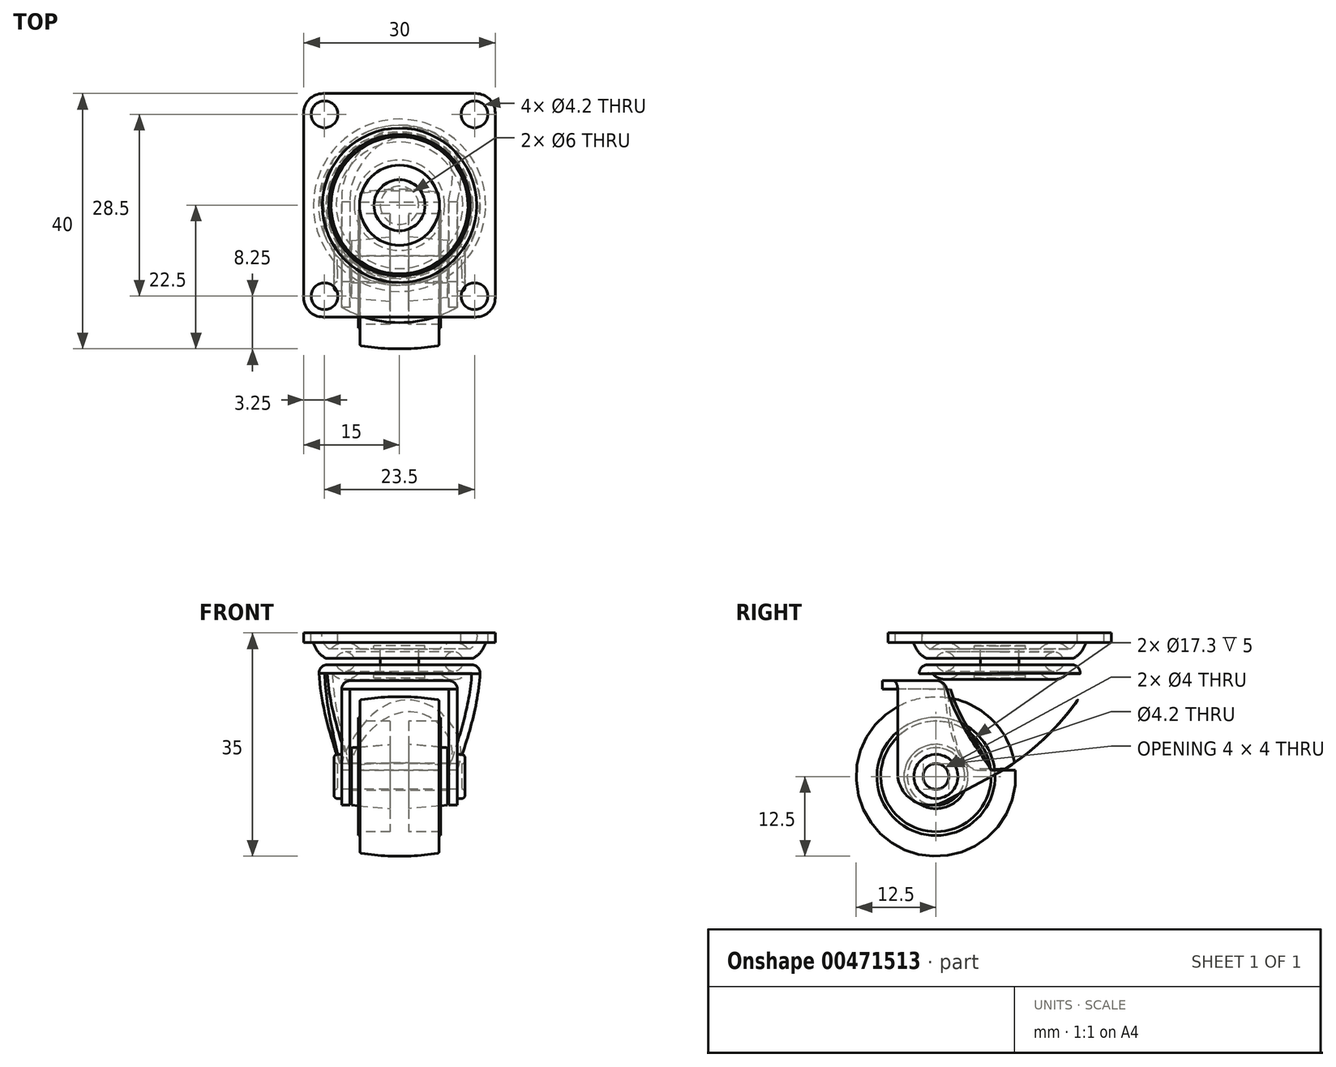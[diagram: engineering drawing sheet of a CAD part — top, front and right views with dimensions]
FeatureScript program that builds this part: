
annotation { "Feature Type Name" : "Feature", "Feature Type Description" : "" }
export const myFeature = defineFeature(function(context is Context, id is Id, definition is map)
    precondition{}
    {
        {
            var Q0;
            Q0=qCreatedBy(makeId("Top.planeOp"),FACE);
            var sketch = newSketch(context, id + "F0", { "sketchPlane" : qUnion([Q0])});
            skLineSegment(sketch, "E0.bottom", {"start": v(15, 17.5) * mm, "end": v(-15, 17.5) * mm});
            skLineSegment(sketch, "E0.top", {"start": v(15, -17.5) * mm, "end": v(-15, -17.5) * mm});
            skLineSegment(sketch, "E0.left", {"start": v(15, 17.5) * mm, "end": v(15, -17.5) * mm});
            skLineSegment(sketch, "E0.right", {"start": v(-15, 17.5) * mm, "end": v(-15, -17.5) * mm});
            skPoint(sketch, "E0.middle", {"position": v(0, 0) * mm});
            skSolve(sketch);
        }
        {
            var Q0;
            Q0=makeQuery(id+"F0.imprint","IMPRINT",FACE,{"disambiguationData":[TD([[makeQuery(id+"F0.imprint","IMPRINT",EDGE,{"derivedFrom":sQuery(id+"F0.wireOp",EDGE,"E0.bottom")}),1.0]])]});
            extrude(context, id + "F1", {"entities" : qUnion([Q0]), "oppositeDirection" : true, "depth" : 1.5 * mm});
        }
        {
            var Q0;
            Q0=qCreatedBy(makeId("Right.planeOp"),FACE);
            var sketch = newSketch(context, id + "F2", { "sketchPlane" : qUnion([Q0])});
            skLineSegment(sketch, "E1", {"start": v(0, -4) * mm, "end": v(0, 0) * mm});
            skLineSegment(sketch, "E2", {"start": v(-11.5, -4) * mm, "end": v(0, -4) * mm});
            skLineSegment(sketch, "E3", {"start": v(-13.5, -1.5) * mm, "end": v(-11.5, -4) * mm, "construction": true});
            skArc(sketch, "E4", {"start": v(-13.5, -1.5) * mm, "mid": v(-12.76, -2.96) * mm, "end": v(-11.5, -4) * mm});
            skLineSegment(sketch, "E5.0", {"start": v(17.5, -1.5) * mm, "end": v(-17.5, -1.5) * mm});
            skSolve(sketch);
        }
        {
            var Q0;
            {var subQ0=sQuery(id+"F2.wireOp",EDGE,"E2");Q0=makeQuery(id+"F2.imprint","IMPRINT",FACE,{"disambiguationData":[TD([[makeQuery(id+"F2.imprint","IMPRINT",EDGE,{"derivedFrom":subQ0}),1.0]])]});}
            var Q1;
            Q1=sQuery(id+"F2.wireOp",EDGE,"E1");
            revolve(context, id + "F3", {"operationType" : NewBodyOperationType.ADD, "entities" : qUnion([Q0]), "axis" : qUnion([Q1]), "revolveType" : RevolveType.FULL});
        }
        {
            var Q0;
            Q0=makeQuery(id+"F1.opExtrude","CAP_FACE",FACE,{"disambiguationData":[OSD([sQuery(id+"F0.wireOp",EDGE,"E0.bottom"),sQuery(id+"F0.wireOp",EDGE,"E0.top"),sQuery(id+"F0.wireOp",EDGE,"E0.left"),sQuery(id+"F0.wireOp",EDGE,"E0.right")])],"isStart":true});
            var sketch = newSketch(context, id + "F4", { "sketchPlane" : qUnion([Q0])});
            skLineSegment(sketch, "E6.bottom", {"start": v(-11.75, 14.25) * mm, "end": v(11.75, 14.25) * mm, "construction": true});
            skLineSegment(sketch, "E6.top", {"start": v(-11.75, -14.25) * mm, "end": v(11.75, -14.25) * mm, "construction": true});
            skLineSegment(sketch, "E6.left", {"start": v(-11.75, 14.25) * mm, "end": v(-11.75, -14.25) * mm, "construction": true});
            skLineSegment(sketch, "E6.right", {"start": v(11.75, 14.25) * mm, "end": v(11.75, -14.25) * mm, "construction": true});
            skPoint(sketch, "E6.middle", {"position": v(0, 0) * mm});
            skCircle(sketch, "E7", {"center": v(-11.75, 14.25) * mm, "radius": 2.1 * mm});
            skCircle(sketch, "E8", {"center": v(11.75, 14.25) * mm, "radius": 2.1 * mm});
            skCircle(sketch, "E9", {"center": v(-11.75, -14.25) * mm, "radius": 2.1 * mm});
            skCircle(sketch, "E10", {"center": v(11.75, -14.25) * mm, "radius": 2.1 * mm});
            skSolve(sketch);
        }
        {
            var Q0;
            Q0=makeQuery(id+"F4.imprint","IMPRINT",FACE,{"disambiguationData":[TD([[makeQuery(id+"F4.imprint","IMPRINT",EDGE,{"derivedFrom":sQuery(id+"F4.wireOp",EDGE,"E9")}),1.0]])]});
            var Q1;
            Q1=makeQuery(id+"F4.imprint","IMPRINT",FACE,{"disambiguationData":[TD([[makeQuery(id+"F4.imprint","IMPRINT",EDGE,{"derivedFrom":sQuery(id+"F4.wireOp",EDGE,"E10")}),1.0]])]});
            var Q2;
            Q2=makeQuery(id+"F4.imprint","IMPRINT",FACE,{"disambiguationData":[TD([[makeQuery(id+"F4.imprint","IMPRINT",EDGE,{"derivedFrom":sQuery(id+"F4.wireOp",EDGE,"E8")}),1.0]])]});
            var Q3;
            Q3=makeQuery(id+"F4.imprint","IMPRINT",FACE,{"disambiguationData":[TD([[makeQuery(id+"F4.imprint","IMPRINT",EDGE,{"derivedFrom":sQuery(id+"F4.wireOp",EDGE,"E7")}),1.0]])]});
            extrude(context, id + "F5", {"entities" : qUnion([Q0, Q1, Q2, Q3]), "operationType" : NewBodyOperationType.REMOVE, "endBound" : BoundingType.THROUGH_ALL, "oppositeDirection" : true, "depth" : 25 * mm});
        }
        {
            var Q0;
            Q0=makeQuery(id+"F1.opExtrude","SWEPT_EDGE",EDGE,{"disambiguationData":[OSD([sQuery(id+"F0.wireOp",EDGE,"E0.top"),sQuery(id+"F0.wireOp",EDGE,"E0.right")])]});
            var Q1;
            Q1=makeQuery(id+"F1.opExtrude","SWEPT_EDGE",EDGE,{"disambiguationData":[OSD([sQuery(id+"F0.wireOp",EDGE,"E0.top"),sQuery(id+"F0.wireOp",EDGE,"E0.left")])]});
            var Q2;
            Q2=makeQuery(id+"F1.opExtrude","SWEPT_EDGE",EDGE,{"disambiguationData":[OSD([sQuery(id+"F0.wireOp",EDGE,"E0.bottom"),sQuery(id+"F0.wireOp",EDGE,"E0.left")])]});
            var Q3;
            Q3=makeQuery(id+"F1.opExtrude","SWEPT_EDGE",EDGE,{"disambiguationData":[OSD([sQuery(id+"F0.wireOp",EDGE,"E0.bottom"),sQuery(id+"F0.wireOp",EDGE,"E0.right")])]});
            fillet(context, id + "F6", {"entities" : qUnion([Q0, Q1, Q2, Q3]), "radius" : 3 * mm, "tangentPropagation" : true, "allowEdgeOverflow" : false});
        }
        {
            var Q0;
            Q0=qCreatedBy(makeId("Front.planeOp"),FACE);
            cPlane(context, id + "F7", {"entities" : qUnion([Q0]), "cplaneType" : CPlaneType.OFFSET, "offset" : 10 * mm, "width" : 150 * mm, "height" : 150 * mm});
        }
        {
            var Q0;
            Q0=qCreatedBy(id+"F7.planeOp",FACE);
            var sketch = newSketch(context, id + "F8", { "sketchPlane" : qUnion([Q0])});
            skArc(sketch, "E11", {"start": v(6.2, -10.5) * mm, "mid": v(0, -10) * mm, "end": v(-6.21, -10.5) * mm});
            skLineSegment(sketch, "E12", {"start": v(-6.46, -13.85) * mm, "end": v(-1.46, -13.85) * mm});
            skLineSegment(sketch, "E13", {"start": v(-7.5, -22.5) * mm, "end": v(7.5, -22.5) * mm});
            skLineSegment(sketch, "E14", {"start": v(1.46, -13.85) * mm, "end": v(6.46, -13.85) * mm});
            skLineSegment(sketch, "E15", {"start": v(-1.46, -13.85) * mm, "end": v(-1.46, -17.47) * mm});
            skLineSegment(sketch, "E16", {"start": v(-7.5, -18) * mm, "end": v(-7.5, -22.5) * mm});
            skLineSegment(sketch, "E17", {"start": v(1.46, -13.85) * mm, "end": v(1.46, -17.47) * mm});
            skLineSegment(sketch, "E18", {"start": v(7.5, -18) * mm, "end": v(7.5, -22.5) * mm});
            skLineSegment(sketch, "E19", {"start": v(0, 0) * mm, "end": v(0, -32.65) * mm, "construction": true});
            skLineSegment(sketch, "E20", {"start": v(-6.21, -10.5) * mm, "end": v(-6.21, -13.25) * mm});
            skLineSegment(sketch, "E21", {"start": v(-6.21, -13.25) * mm, "end": v(-6.46, -13.25) * mm});
            skLineSegment(sketch, "E22", {"start": v(-6.46, -13.25) * mm, "end": v(-6.46, -13.85) * mm});
            skLineSegment(sketch, "E23", {"start": v(6.2, -10.5) * mm, "end": v(6.2, -13.25) * mm});
            skLineSegment(sketch, "E24", {"start": v(6.21, -13.25) * mm, "end": v(6.46, -13.25) * mm});
            skLineSegment(sketch, "E25", {"start": v(6.46, -13.25) * mm, "end": v(6.46, -13.85) * mm});
            skLineSegment(sketch, "E26", {"start": v(-7.5, -18) * mm, "end": v(-1.46, -17.47) * mm});
            skLineSegment(sketch, "E27", {"start": v(7.5, -18) * mm, "end": v(1.46, -17.47) * mm});
            skSolve(sketch);
        }
        {
            var Q0;
            Q0=makeQuery(id+"F8.imprint","IMPRINT",FACE,{"disambiguationData":[TD([[makeQuery(id+"F8.imprint","IMPRINT",EDGE,{"derivedFrom":sQuery(id+"F8.wireOp",EDGE,"E11")}),1.0]])]});
            var Q1;
            Q1=sQuery(id+"F8.wireOp",EDGE,"E13");
            revolve(context, id + "F9", {"entities" : qUnion([Q0]), "axis" : qUnion([Q1]), "revolveType" : RevolveType.FULL});
        }
        {
            var Q0;
            Q0=makeQuery(id+"F9.opRevolve","SWEPT_FACE",FACE,{"disambiguationData":[OSD([sQuery(id+"F8.wireOp",EDGE,"E18")])]});
            var sketch = newSketch(context, id + "F10", { "sketchPlane" : qUnion([Q0])});
            skCircle(sketch, "E28", {"center": v(-10, -22.5) * mm, "radius": 2.1 * mm});
            skSolve(sketch);
        }
        {
            var Q0;
            Q0=makeQuery(id+"F10.imprint","IMPRINT",FACE,{"disambiguationData":[TD([[makeQuery(id+"F10.imprint","IMPRINT",EDGE,{"derivedFrom":sQuery(id+"F10.wireOp",EDGE,"E28")}),1.0]])]});
            extrude(context, id + "F11", {"entities" : qUnion([Q0]), "operationType" : NewBodyOperationType.REMOVE, "endBound" : BoundingType.THROUGH_ALL, "oppositeDirection" : true, "depth" : 25 * mm});
        }
        {
            var Q0;
            Q0=makeQuery(id+"F9.opRevolve","SWEPT_EDGE",EDGE,{"disambiguationData":[OSD([sQuery(id+"F8.wireOp",EDGE,"E11"),sQuery(id+"F8.wireOp",EDGE,"E23")])]});
            var Q1;
            Q1=makeQuery(id+"F9.opRevolve","SWEPT_EDGE",EDGE,{"disambiguationData":[OSD([sQuery(id+"F8.wireOp",EDGE,"E11"),sQuery(id+"F8.wireOp",EDGE,"E20")])]});
            fillet(context, id + "F12", {"entities" : qUnion([Q0, Q1]), "radius" : 0.3 * mm, "tangentPropagation" : true, "allowEdgeOverflow" : false});
        }
        {
            var Q0;
            Q0=makeQuery(id+"F1.opExtrude","CAP_FACE",FACE,{"disambiguationData":[OSD([sQuery(id+"F0.wireOp",EDGE,"E0.bottom"),sQuery(id+"F0.wireOp",EDGE,"E0.top"),sQuery(id+"F0.wireOp",EDGE,"E0.left"),sQuery(id+"F0.wireOp",EDGE,"E0.right")])],"isStart":true});
            cPlane(context, id + "F13", {"entities" : qUnion([Q0]), "cplaneType" : CPlaneType.OFFSET, "offset" : 5 * mm, "oppositeDirection" : true, "width" : 150 * mm, "height" : 150 * mm});
        }
        {
            var Q0;
            Q0=qCreatedBy(id+"F13.planeOp",FACE);
            var sketch = newSketch(context, id + "F14", { "sketchPlane" : qUnion([Q0])});
            skCircle(sketch, "E29", {"center": v(0, 0) * mm, "radius": 12.65 * mm});
            skSolve(sketch);
        }
        {
            var Q0;
            Q0=qCreatedBy(id+"F13.planeOp",FACE);
            cPlane(context, id + "F15", {"entities" : qUnion([Q0]), "cplaneType" : CPlaneType.OFFSET, "offset" : 15 * mm, "oppositeDirection" : true, "width" : 150 * mm, "height" : 150 * mm});
        }
        {
            var Q0;
            Q0=qCreatedBy(id+"F15.planeOp",FACE);
            var sketch = newSketch(context, id + "F16", { "sketchPlane" : qUnion([Q0])});
            skArc(sketch, "E30", {"start": v(-9.05, -3.6) * mm, "mid": v(0, -12.65) * mm, "end": v(9.05, -3.6) * mm});
            skArc(sketch, "E31", {"start": v(9.05, 3.6) * mm, "mid": v(0, 12.65) * mm, "end": v(-9.05, 3.6) * mm});
            skLineSegment(sketch, "E32", {"start": v(-9.05, -3.6) * mm, "end": v(-9.05, 3.6) * mm});
            skLineSegment(sketch, "E33", {"start": v(9.05, -3.6) * mm, "end": v(9.05, 3.6) * mm});
            skSolve(sketch);
        }
        {
            var Q0;
            Q0=qCreatedBy(id+"F13.planeOp",FACE);
            cPlane(context, id + "F17", {"entities" : qUnion([Q0]), "cplaneType" : CPlaneType.OFFSET, "offset" : 3 * mm, "oppositeDirection" : true, "width" : 150 * mm, "height" : 150 * mm});
        }
        {
            var Q0;
            Q0=qCreatedBy(id+"F17.planeOp",FACE);
            var sketch = newSketch(context, id + "F18", { "sketchPlane" : qUnion([Q0])});
            skCircle(sketch, "E34", {"center": v(0, 0) * mm, "radius": 12.65 * mm});
            skSolve(sketch);
        }
        {
            var Q0;
            Q0=makeQuery(id+"F14.imprint","IMPRINT",FACE,{"disambiguationData":[TD([[makeQuery(id+"F14.imprint","IMPRINT",EDGE,{"derivedFrom":sQuery(id+"F14.wireOp",EDGE,"E29")}),1.0]])]});
            var Q1;
            Q1=makeQuery(id+"F18.imprint","IMPRINT",FACE,{"disambiguationData":[TD([[makeQuery(id+"F18.imprint","IMPRINT",EDGE,{"derivedFrom":sQuery(id+"F18.wireOp",EDGE,"E34")}),1.0]])]});
            var Q2;
            Q2=makeQuery(id+"F16.imprint","IMPRINT",FACE,{"disambiguationData":[TD([[makeQuery(id+"F16.imprint","IMPRINT",EDGE,{"derivedFrom":sQuery(id+"F16.wireOp",EDGE,"E30")}),1.0]])]});
            loft(context, id + "F19", {"endCondition" : LoftEndDerivativeType.TANGENT_TO_PROFILE, "endMagnitude" : 0.5, "sheetProfilesArray" : [{ "sheetProfileEntities" : qUnion([Q0]) }, { "sheetProfileEntities" : qUnion([Q1]) }, { "sheetProfileEntities" : qUnion([Q2]) }]});
        }
        {
            var Q0;
            Q0=makeQuery(id+"F19.opLoft","SWEPT_BODY",BODY,{"disambiguationData":[OSD([makeQuery(id+"F14.imprint","IMPRINT",FACE,{"disambiguationData":[TD([[makeQuery(id+"F14.imprint","IMPRINT",EDGE,{"derivedFrom":sQuery(id+"F14.wireOp",EDGE,"E29")}),1.0]])]}),makeQuery(id+"F16.imprint","IMPRINT",FACE,{"disambiguationData":[TD([[makeQuery(id+"F16.imprint","IMPRINT",EDGE,{"derivedFrom":sQuery(id+"F16.wireOp",EDGE,"E30")}),1.0]])]}),sQuery(id+"F18.wireOp",EDGE,"E34")])]});
            deleteBodies(context, id + "F20", {"entities" : qUnion([Q0])});
        }
        {
            var Q0;
            Q0=qCreatedBy(makeId("Right.planeOp"),FACE);
            var sketch = newSketch(context, id + "F21", { "sketchPlane" : qUnion([Q0])});
            skLineSegment(sketch, "E35", {"start": v(0.5, -7.5) * mm, "end": v(-16, -7.5) * mm});
            skLineSegment(sketch, "E36", {"start": v(-16, -7.5) * mm, "end": v(-16, -22) * mm});
            skLineSegment(sketch, "E37", {"start": v(-16, -27) * mm, "end": v(-4.2, -27) * mm});
            skLineSegment(sketch, "E38", {"start": v(0.5, -21.5) * mm, "end": v(0.5, -7.5) * mm});
            skArc(sketch, "E39", {"start": v(-16, -22) * mm, "mid": v(-13.57, -26.3) * mm, "end": v(-8.63, -26.4) * mm});
            skLineSegment(sketch, "E40", {"start": v(0.5, -21.5) * mm, "end": v(-8.63, -26.4) * mm});
            skLineSegment(sketch, "E41", {"start": v(-16, -21.5) * mm, "end": v(0.5, -21.5) * mm, "construction": true});
            skPoint(sketch, "E42.0", {"position": v(-17.5, -1.5) * mm});
            skSolve(sketch);
        }
        {
            var Q0;
            Q0=makeQuery(id+"F21.imprint","IMPRINT",FACE,{"disambiguationData":[TD([[makeQuery(id+"F21.imprint","IMPRINT",EDGE,{"derivedFrom":sQuery(id+"F21.wireOp",EDGE,"E35")}),1.0]])]});
            extrude(context, id + "F22", {"entities" : qUnion([Q0]), "endBound" : BoundingType.SYMMETRIC, "depth" : 18.1 * mm});
        }
        {
            var Q0;
            Q0=makeQuery(id+"F1.opExtrude","CAP_FACE",FACE,{"disambiguationData":[OSD([sQuery(id+"F0.wireOp",EDGE,"E0.bottom"),sQuery(id+"F0.wireOp",EDGE,"E0.top"),sQuery(id+"F0.wireOp",EDGE,"E0.left"),sQuery(id+"F0.wireOp",EDGE,"E0.right")])],"isStart":true});
            cPlane(context, id + "F23", {"entities" : qUnion([Q0]), "cplaneType" : CPlaneType.OFFSET, "offset" : 5 * mm, "oppositeDirection" : true, "width" : 150 * mm, "height" : 150 * mm});
        }
        {
            var Q0;
            Q0=qCreatedBy(id+"F23.planeOp",FACE);
            var sketch = newSketch(context, id + "F24", { "sketchPlane" : qUnion([Q0])});
            skCircle(sketch, "E43", {"center": v(0, 0) * mm, "radius": 12.65 * mm});
            skSolve(sketch);
        }
        {
            var Q0;
            Q0=makeQuery(id+"F1.opExtrude","CAP_FACE",FACE,{"disambiguationData":[OSD([sQuery(id+"F0.wireOp",EDGE,"E0.bottom"),sQuery(id+"F0.wireOp",EDGE,"E0.top"),sQuery(id+"F0.wireOp",EDGE,"E0.left"),sQuery(id+"F0.wireOp",EDGE,"E0.right")])],"isStart":true});
            cPlane(context, id + "F25", {"entities" : qUnion([Q0]), "cplaneType" : CPlaneType.OFFSET, "offset" : 21.5 * mm, "oppositeDirection" : true, "width" : 150 * mm, "height" : 150 * mm});
        }
        {
            var Q0;
            Q0=qCreatedBy(id+"F25.planeOp",FACE);
            var sketch = newSketch(context, id + "F26", { "sketchPlane" : qUnion([Q0])});
            skPoint(sketch, "E44.middle", {"position": v(0, 0) * mm});
            skCircle(sketch, "E45", {"center": v(0, 0) * mm, "radius": 12.65 * mm, "construction": true});
            skLineSegment(sketch, "E46", {"start": v(-9.05, -3.6) * mm, "end": v(-9.05, 3.6) * mm});
            skLineSegment(sketch, "E47", {"start": v(9.05, -3.6) * mm, "end": v(9.05, 3.6) * mm});
            skLineSegment(sketch, "E48", {"start": v(0, -12.65) * mm, "end": v(0, 12.65) * mm, "construction": true});
            skArc(sketch, "E49", {"start": v(-9.05, -3.6) * mm, "mid": v(0, -12.65) * mm, "end": v(9.05, -3.6) * mm});
            skArc(sketch, "E50", {"start": v(-9.05, 3.6) * mm, "mid": v(0, 12.65) * mm, "end": v(9.05, 3.6) * mm});
            skSolve(sketch);
        }
        {
            var Q0;
            Q0 = qSketchRegion(id + "F24", true);
            var Q1;
            Q1 = qSketchRegion(id + "F26", true);
            loft(context, id + "F27", {"startCondition" : LoftEndDerivativeType.NORMAL_TO_PROFILE, "startMagnitude" : 1, "sheetProfilesArray" : [{ "sheetProfileEntities" : qUnion([Q0]) }, { "sheetProfileEntities" : qUnion([Q1]) }]});
        }
        {
            var Q0;
            Q0=makeQuery(id+"F27.opLoft","SWEPT_BODY",BODY,{"disambiguationData":[OSD([makeQuery(id+"F24.imprint","IMPRINT",FACE,{"disambiguationData":[TD([[makeQuery(id+"F24.imprint","IMPRINT",EDGE,{"derivedFrom":sQuery(id+"F24.wireOp",EDGE,"E43")}),1.0]])]}),makeQuery(id+"F26.imprint","IMPRINT",FACE,{"disambiguationData":[TD([[makeQuery(id+"F26.imprint","IMPRINT",EDGE,{"derivedFrom":sQuery(id+"F26.wireOp",EDGE,"E46")}),-1.0]])]})])]});
            var Q1;
            Q1=makeQuery(id+"F22.opExtrude","SWEPT_BODY",BODY,{"disambiguationData":[OSD([sQuery(id+"F21.wireOp",EDGE,"E35"),sQuery(id+"F21.wireOp",EDGE,"E36"),sQuery(id+"F21.wireOp",EDGE,"E38"),sQuery(id+"F21.wireOp",EDGE,"E39"),sQuery(id+"F21.wireOp",EDGE,"E40")])]});
            booleanBodies(context, id + "F28", {"operationType" : BooleanOperationType.UNION, "tools" : qUnion([Q0, Q1])});
        }
        {
            var Q0;
            Q0=makeQuery(id+"F27.opLoft","CAP_FACE",FACE,{"disambiguationData":[OSD([makeQuery(id+"F26.imprint","IMPRINT",FACE,{"disambiguationData":[TD([[makeQuery(id+"F26.imprint","IMPRINT",EDGE,{"derivedFrom":sQuery(id+"F26.wireOp",EDGE,"E46")}),-1.0]])]})])],"isStart":true});
            var Q1;
            Q1=makeQuery(id+"F22.opExtrude","SWEPT_FACE",FACE,{"disambiguationData":[OSD([sQuery(id+"F21.wireOp",EDGE,"E40")])]});
            var Q2;
            Q2=makeQuery(id+"F22.opExtrude","SWEPT_FACE",FACE,{"disambiguationData":[OSD([sQuery(id+"F21.wireOp",EDGE,"E39")])]});
            var Q3;
            Q3=makeQuery(id+"F22.opExtrude","SWEPT_FACE",FACE,{"disambiguationData":[OSD([sQuery(id+"F21.wireOp",EDGE,"E36")])]});
            shell(context, id + "F29", {"entities" : qUnion([Q0, Q1, Q2, Q3]), "thickness" : 1.3 * mm});
        }
        {
            var Q0;
            Q0=qCreatedBy(makeId("Right.planeOp"),FACE);
            var sketch = newSketch(context, id + "F30", { "sketchPlane" : qUnion([Q0])});
            skArc(sketch, "E51", {"start": v(0.5, -21.5) * mm, "mid": v(7.1, -16.43) * mm, "end": v(12.5, -10.1) * mm});
            skLineSegment(sketch, "E52.0", {"start": v(0.5, -21.5) * mm, "end": v(-8.63, -26.4) * mm, "construction": true});
            skLineSegment(sketch, "E53", {"start": v(12.5, -10.1) * mm, "end": v(14.5, -10.1) * mm});
            skLineSegment(sketch, "E54", {"start": v(14.5, -10.1) * mm, "end": v(14.5, -21.5) * mm});
            skLineSegment(sketch, "E55", {"start": v(14.5, -21.5) * mm, "end": v(0.5, -21.5) * mm});
            skSolve(sketch);
        }
        {
            var Q0;
            Q0=makeQuery(id+"F30.imprint","IMPRINT",FACE,{"disambiguationData":[TD([[makeQuery(id+"F30.imprint","IMPRINT",EDGE,{"derivedFrom":sQuery(id+"F30.wireOp",EDGE,"E51")}),-1.0]])]});
            extrude(context, id + "F31", {"entities" : qUnion([Q0]), "operationType" : NewBodyOperationType.REMOVE, "endBound" : BoundingType.SYMMETRIC, "oppositeDirection" : true, "depth" : 25 * mm});
        }
        {
            var Q0;
            Q0=makeQuery(id+"F22.opExtrude","SWEPT_FACE",FACE,{"disambiguationData":[OSD([sQuery(id+"F21.wireOp",EDGE,"E35")])]});
            var sketch = newSketch(context, id + "F32", { "sketchPlane" : qUnion([Q0])});
            skLineSegment(sketch, "E56.0", {"start": v(9.05, -16) * mm, "end": v(-9.05, -16) * mm});
            skArc(sketch, "E57", {"start": v(-9.05, -16) * mm, "mid": v(0, -18.38) * mm, "end": v(9.05, -16) * mm});
            skSolve(sketch);
        }
        {
            var Q0;
            Q0=makeQuery(id+"F32.imprint","IMPRINT",FACE,{"disambiguationData":[TD([[makeQuery(id+"F32.imprint","IMPRINT",EDGE,{"derivedFrom":sQuery(id+"F32.wireOp",EDGE,"E56.0")}),1.0]])]});
            var Q1;
            Q1=makeQuery(id+"F29.opShell","OFFSET_FACE",FACE,{"disambiguationData":[OSD([sQuery(id+"F21.wireOp",EDGE,"E35")])]});
            extrude(context, id + "F33", {"entities" : qUnion([Q0]), "operationType" : NewBodyOperationType.ADD, "endBound" : BoundingType.UP_TO_SURFACE, "oppositeDirection" : true, "endBoundEntityFace" : qUnion([Q1]), "depth" : 25 * mm});
        }
        {
            var Q0;
            Q0=makeQuery(id+"F27.opLoft","CAP_FACE",FACE,{"disambiguationData":[OSD([makeQuery(id+"F24.imprint","IMPRINT",FACE,{"disambiguationData":[TD([[makeQuery(id+"F24.imprint","IMPRINT",EDGE,{"derivedFrom":sQuery(id+"F24.wireOp",EDGE,"E43")}),1.0]])]})])],"isStart":true});
            var Q1;
            Q1=makeQuery(id+"F22.opExtrude","CAP_EDGE",EDGE,{"disambiguationData":[OSD([sQuery(id+"F21.wireOp",EDGE,"E35")])],"isStart":false});
            var Q2;
            Q2=makeQuery(id+"F22.opExtrude","CAP_EDGE",EDGE,{"disambiguationData":[OSD([sQuery(id+"F21.wireOp",EDGE,"E35")])],"isStart":true});
            fillet(context, id + "F34", {"entities" : qUnion([Q0, Q1, Q2]), "radius" : 1.3 * mm, "tangentPropagation" : true, "allowEdgeOverflow" : false});
        }
        {
            var Q0;
            Q0=qCreatedBy(id+"F7.planeOp",FACE);
            var sketch = newSketch(context, id + "F35", { "sketchPlane" : qUnion([Q0])});
            skLineSegment(sketch, "E58.0", {"start": v(-7.5, -20.4) * mm, "end": v(-7.5, -24.6) * mm});
            skLineSegment(sketch, "E59.0", {"start": v(7.5, -20.4) * mm, "end": v(7.5, -24.6) * mm});
            skLineSegment(sketch, "E60", {"start": v(-9.75, -22.5) * mm, "end": v(9.75, -22.5) * mm});
            skLineSegment(sketch, "E61", {"start": v(-9.05, -20.5) * mm, "end": v(9.05, -20.5) * mm});
            skPoint(sketch, "E62", {"position": v(-7.5, -22.5) * mm});
            skLineSegment(sketch, "E63", {"start": v(-9.05, -20.5) * mm, "end": v(-9.05, -19.05) * mm});
            skLineSegment(sketch, "E64", {"start": v(-9.05, -19.05) * mm, "end": v(-10.25, -19.05) * mm});
            skLineSegment(sketch, "E65", {"start": v(-10.25, -19.05) * mm, "end": v(-10.25, -20.5) * mm});
            skLineSegment(sketch, "E66.0.0", {"start": v(-9.05, -22) * mm, "end": v(-9.05, -8.8) * mm});
            skFitSpline(sketch, "E66.0.2", {"points": [v(-9.05, -21.5) * mm, v(-9.05, -17.27) * mm, v(-9.05, -13.03) * mm, v(-9.05, -8.8) * mm], "construction": true});
            skLineSegment(sketch, "E66.0.4", {"start": v(-9.05, -21.5) * mm, "end": v(-9.05, -26.4) * mm});
            skLineSegment(sketch, "E66.0.5", {"start": v(-9.05, -27) * mm, "end": v(-9.05, -22) * mm, "construction": true});
            skLineSegment(sketch, "E67.0", {"start": v(-9.05, -21.5) * mm, "end": v(-9.05, -26.4) * mm, "construction": true});
            skLineSegment(sketch, "E68", {"start": v(-10.25, -20.5) * mm, "end": v(-9.75, -20.5) * mm});
            skLineSegment(sketch, "E69", {"start": v(-9.75, -20.5) * mm, "end": v(-9.75, -22.5) * mm});
            skLineSegment(sketch, "E70", {"start": v(0, -7.68) * mm, "end": v(0, -37.41) * mm, "construction": true});
            skLineSegment(sketch, "E71.MirrorCS", {"start": v(10.25, -20.5) * mm, "end": v(9.75, -20.5) * mm});
            skLineSegment(sketch, "E72.MirrorCS", {"start": v(9.75, -20.5) * mm, "end": v(9.75, -22.5) * mm});
            skLineSegment(sketch, "E73.MirrorCS", {"start": v(10.25, -19.05) * mm, "end": v(10.25, -20.5) * mm});
            skLineSegment(sketch, "E74.MirrorCS", {"start": v(9.05, -20.5) * mm, "end": v(9.05, -19.05) * mm});
            skLineSegment(sketch, "E75.MirrorCS", {"start": v(9.05, -19.05) * mm, "end": v(10.25, -19.05) * mm});
            skSolve(sketch);
        }
        {
            var Q0;
            {var subQ4=sQuery(id+"F35.wireOp",EDGE,"E64");Q0=makeQuery(id+"F35.imprint","IMPRINT",FACE,{"disambiguationData":[TD([[makeQuery(id+"F35.imprint","IMPRINT",EDGE,{"derivedFrom":subQ4}),1.0]])]});}
            var Q1;
            {var subQ3=sQuery(id+"F35.wireOp",EDGE,"E66.0.4");var subQ10=makeQuery(id+"F35.imprint","IMPRINT",VERTEX,{"derivedFrom":subQ3});Q1=makeQuery(id+"F35.imprint","IMPRINT",FACE,{"disambiguationData":[TD([[makeQuery(id+"F35.imprint","IMPRINT",EDGE,{"disambiguationData":[TD([[subQ10,1.0]])],"derivedFrom":subQ3}),1.0]])]});}
            var Q2;
            {var subQ0=sQuery(id+"F35.wireOp",EDGE,"E60");var subQ1=sQuery(id+"F35.wireOp",EDGE,"E58.0");var subQ2=makeQuery(id+"F35.imprint","INTERSECT",VERTEX,{"derivedFrom":[subQ1,subQ0]});Q2=makeQuery(id+"F35.imprint","IMPRINT",FACE,{"disambiguationData":[TD([[makeQuery(id+"F35.imprint","IMPRINT",EDGE,{"disambiguationData":[TD([[subQ2,1.0]])],"derivedFrom":subQ1}),1.0]])]});}
            var Q3;
            Q3=makeQuery(id+"F35.imprint","IMPRINT",FACE,{"disambiguationData":[TD([[makeQuery(id+"F35.imprint","IMPRINT",EDGE,{"derivedFrom":sQuery(id+"F35.wireOp",EDGE,"E71.MirrorCS")}),-1.0]])]});
            var Q4;
            Q4=sQuery(id+"F35.wireOp",EDGE,"E60");
            revolve(context, id + "F36", {"entities" : qUnion([Q0, Q1, Q2, Q3]), "axis" : qUnion([Q4]), "revolveType" : RevolveType.FULL});
        }
        {
            var Q0;
            Q0=makeQuery(id+"F36.opRevolve","SWEPT_EDGE",EDGE,{"disambiguationData":[OSD([sQuery(id+"F35.wireOp",EDGE,"E73.MirrorCS"),sQuery(id+"F35.wireOp",EDGE,"E75.MirrorCS")])]});
            var Q1;
            Q1=makeQuery(id+"F36.opRevolve","SWEPT_EDGE",EDGE,{"disambiguationData":[OSD([sQuery(id+"F35.wireOp",EDGE,"E71.MirrorCS"),sQuery(id+"F35.wireOp",EDGE,"E73.MirrorCS")])]});
            var Q2;
            Q2=makeQuery(id+"F36.opRevolve","SWEPT_EDGE",EDGE,{"disambiguationData":[OSD([sQuery(id+"F35.wireOp",EDGE,"E65"),sQuery(id+"F35.wireOp",EDGE,"E68")])]});
            var Q3;
            Q3=makeQuery(id+"F36.opRevolve","SWEPT_EDGE",EDGE,{"disambiguationData":[OSD([sQuery(id+"F35.wireOp",EDGE,"E64"),sQuery(id+"F35.wireOp",EDGE,"E65")])]});
            fillet(context, id + "F37", {"entities" : qUnion([Q0, Q1, Q2, Q3]), "radius" : 0.5 * mm, "tangentPropagation" : true, "allowEdgeOverflow" : false});
        }
        {
            var Q0;
            Q0=makeQuery(id+"F36.opRevolve","SWEPT_BODY",BODY,{"disambiguationData":[OSD([sQuery(id+"F35.wireOp",EDGE,"E60"),sQuery(id+"F35.wireOp",EDGE,"E61"),sQuery(id+"F35.wireOp",EDGE,"E64"),sQuery(id+"F35.wireOp",EDGE,"E65"),sQuery(id+"F35.wireOp",EDGE,"E66.0.0"),sQuery(id+"F35.wireOp",EDGE,"E68"),sQuery(id+"F35.wireOp",EDGE,"E69"),sQuery(id+"F35.wireOp",EDGE,"E71.MirrorCS"),sQuery(id+"F35.wireOp",EDGE,"E72.MirrorCS"),sQuery(id+"F35.wireOp",EDGE,"E73.MirrorCS"),sQuery(id+"F35.wireOp",EDGE,"E74.MirrorCS"),sQuery(id+"F35.wireOp",EDGE,"E75.MirrorCS")])]});
            var Q1;
            Q1=makeQuery(id+"F27.opLoft","SWEPT_BODY",BODY,{"disambiguationData":[OSD([makeQuery(id+"F24.imprint","IMPRINT",FACE,{"disambiguationData":[TD([[makeQuery(id+"F24.imprint","IMPRINT",EDGE,{"derivedFrom":sQuery(id+"F24.wireOp",EDGE,"E43")}),1.0]])]}),makeQuery(id+"F26.imprint","IMPRINT",FACE,{"disambiguationData":[TD([[makeQuery(id+"F26.imprint","IMPRINT",EDGE,{"derivedFrom":sQuery(id+"F26.wireOp",EDGE,"E46")}),-1.0]])]})])]});
            booleanBodies(context, id + "F38", {"operationType" : BooleanOperationType.SUBTRACTION, "tools" : qUnion([Q0]), "targets" : qUnion([Q1]), "keepTools" : true});
        }
        {
            var Q0;
            Q0=makeQuery(id+"F3.opRevolve","SWEPT_FACE",FACE,{"disambiguationData":[OSD([sQuery(id+"F2.wireOp",EDGE,"E2")])]});
            var Q1;
            Q1=makeQuery(id+"F27.opLoft","CAP_FACE",FACE,{"disambiguationData":[OSD([makeQuery(id+"F24.imprint","IMPRINT",FACE,{"disambiguationData":[TD([[makeQuery(id+"F24.imprint","IMPRINT",EDGE,{"derivedFrom":sQuery(id+"F24.wireOp",EDGE,"E43")}),1.0]])]})])],"isStart":true});
            cPlane(context, id + "F39", {"entities" : qUnion([Q0, Q1]), "cplaneType" : CPlaneType.MID_PLANE, "offset" : 25 * mm, "width" : 150 * mm, "height" : 150 * mm});
        }
        {
            var Q0;
            Q0=qCreatedBy(id+"F39.planeOp",FACE);
            var sketch = newSketch(context, id + "F40", { "sketchPlane" : qUnion([Q0])});
            skArc(sketch, "E76", {"start": v(0, 7) * mm, "mid": v(1.5, 8.5) * mm, "end": v(0, 10) * mm});
            skLineSegment(sketch, "E77", {"start": v(0, 10) * mm, "end": v(0, 7) * mm});
            skSolve(sketch);
        }
        {
            var Q0;
            Q0=makeQuery(id+"F40.imprint","IMPRINT",FACE,{"disambiguationData":[TD([[makeQuery(id+"F40.imprint","IMPRINT",EDGE,{"derivedFrom":sQuery(id+"F40.wireOp",EDGE,"E76")}),1.0]])]});
            var Q1;
            Q1=sQuery(id+"F40.wireOp",EDGE,"E77");
            revolve(context, id + "F41", {"entities" : qUnion([Q0]), "axis" : qUnion([Q1]), "revolveType" : RevolveType.FULL});
        }
        {
            var Q0;
            Q0=makeQuery(id+"F41.opRevolve","SWEPT_BODY",BODY,{"disambiguationData":[OSD([sQuery(id+"F40.wireOp",EDGE,"E76"),sQuery(id+"F40.wireOp",EDGE,"E77")])]});
            var Q1;
            Q1=makeQuery(id+"F3.opRevolve","SWEPT_EDGE",EDGE,{"disambiguationData":[OSD([sQuery(id+"F2.wireOp",EDGE,"E2"),sQuery(id+"F2.wireOp",EDGE,"E4")])]});
            circularPattern(context, id + "F42", {"entities" : qUnion([Q0]), "axis" : qUnion([Q1]), "angle" : 360 * degree, "instanceCount" : 16, "equalSpace" : true});
        }
        {
            var Q0;
            Q0=qCreatedBy(makeId("Right.planeOp"),FACE);
            var sketch = newSketch(context, id + "F43", { "sketchPlane" : qUnion([Q0])});
            skCircle(sketch, "E78", {"center": v(-8.5, -4.5) * mm, "radius": 1.5 * mm});
            skSolve(sketch);
        }
        {
            var Q0;
            Q0 = qSketchRegion(id + "F43", true);
            var Q1;
            Q1=makeQuery(id+"F3.opRevolve","SWEPT_EDGE",EDGE,{"disambiguationData":[OSD([sQuery(id+"F2.wireOp",EDGE,"E2"),sQuery(id+"F2.wireOp",EDGE,"E4")])]});
            revolve(context, id + "F44", {"operationType" : NewBodyOperationType.REMOVE, "entities" : qUnion([Q0]), "axis" : qUnion([Q1]), "revolveType" : RevolveType.FULL});
        }
        {
            var Q0;
            Q0=makeQuery(id+"F1.opExtrude","CAP_FACE",FACE,{"disambiguationData":[OSD([sQuery(id+"F0.wireOp",EDGE,"E0.bottom"),sQuery(id+"F0.wireOp",EDGE,"E0.top"),sQuery(id+"F0.wireOp",EDGE,"E0.left"),sQuery(id+"F0.wireOp",EDGE,"E0.right")])],"isStart":true});
            shell(context, id + "F45", {"entities" : qUnion([Q0]), "thickness" : 1.5 * mm});
        }
        {
            var Q0;
            Q0=qCreatedBy(makeId("Right.planeOp"),FACE);
            var sketch = newSketch(context, id + "F46", { "sketchPlane" : qUnion([Q0])});
            skCircle(sketch, "E79", {"center": v(-8.5, -4.5) * mm, "radius": 1.5 * mm});
            skLineSegment(sketch, "E80", {"start": v(0, 0) * mm, "end": v(0, -11.6) * mm, "construction": true});
            skSolve(sketch);
        }
        {
            var Q0;
            Q0=makeQuery(id+"F46.imprint","IMPRINT",FACE,{"disambiguationData":[TD([[makeQuery(id+"F46.imprint","IMPRINT",EDGE,{"derivedFrom":sQuery(id+"F46.wireOp",EDGE,"E79")}),1.0]])]});
            var Q1;
            Q1=sQuery(id+"F46.wireOp",EDGE,"E80");
            revolve(context, id + "F47", {"operationType" : NewBodyOperationType.REMOVE, "entities" : qUnion([Q0]), "axis" : qUnion([Q1]), "revolveType" : RevolveType.FULL});
        }
        {
            var Q0;
            Q0=qCreatedBy(makeId("Right.planeOp"),FACE);
            var sketch = newSketch(context, id + "F48", { "sketchPlane" : qUnion([Q0])});
            skArc(sketch, "E81", {"start": v(-8.5, -6) * mm, "mid": v(-7.63, -5.72) * mm, "end": v(-7.09, -5) * mm});
            skLineSegment(sketch, "E82", {"start": v(-8.5, -6) * mm, "end": v(8.5, -6) * mm});
            skArc(sketch, "E83", {"start": v(7.09, -5) * mm, "mid": v(7.63, -5.72) * mm, "end": v(8.5, -6) * mm});
            skArc(sketch, "E84.0", {"start": v(-10.72, -6.2) * mm, "mid": v(-8.5, -7.3) * mm, "end": v(-6.28, -6.2) * mm});
            skLineSegment(sketch, "E85", {"start": v(-10.72, -6.2) * mm, "end": v(-6.28, -6.2) * mm});
            skLineSegment(sketch, "E86", {"start": v(0, 0) * mm, "end": v(0, -7.9) * mm, "construction": true});
            skSolve(sketch);
        }
        {
            var Q0;
            Q0=makeQuery(id+"F48.imprint","IMPRINT",FACE,{"disambiguationData":[TD([[makeQuery(id+"F48.imprint","IMPRINT",EDGE,{"derivedFrom":sQuery(id+"F48.wireOp",EDGE,"E84.0")}),1.0]])]});
            var Q1;
            Q1=sQuery(id+"F48.wireOp",EDGE,"E86");
            revolve(context, id + "F49", {"operationType" : NewBodyOperationType.ADD, "entities" : qUnion([Q0]), "axis" : qUnion([Q1]), "revolveType" : RevolveType.FULL});
        }
        {
            var Q0;
            Q0=qCreatedBy(makeId("Right.planeOp"),FACE);
            var sketch = newSketch(context, id + "F50", { "sketchPlane" : qUnion([Q0])});
            skLineSegment(sketch, "E87", {"start": v(0, -2) * mm, "end": v(0, -7.1) * mm});
            skLineSegment(sketch, "E88", {"start": v(0, -7.1) * mm, "end": v(-4, -7.1) * mm});
            skLineSegment(sketch, "E89", {"start": v(-4, -7.1) * mm, "end": v(-4, -6.6) * mm});
            skLineSegment(sketch, "E90", {"start": v(-4, -6.6) * mm, "end": v(-3, -6.6) * mm});
            skLineSegment(sketch, "E91", {"start": v(-3, -6.6) * mm, "end": v(-3, -2.5) * mm});
            skLineSegment(sketch, "E92", {"start": v(-3, -2.5) * mm, "end": v(-4, -2.5) * mm});
            skLineSegment(sketch, "E93", {"start": v(-4, -2.5) * mm, "end": v(-4, -2) * mm});
            skLineSegment(sketch, "E94", {"start": v(-4, -2) * mm, "end": v(0, -2) * mm});
            skLineSegment(sketch, "E95.0.0", {"start": v(-6.26, -2.5) * mm, "end": v(6.26, -2.5) * mm});
            skLineSegment(sketch, "E96.0.0", {"start": v(6.36, -6.3) * mm, "end": v(-6.36, -6.3) * mm});
            skSolve(sketch);
        }
        {
            var Q0;
            Q0 = qSketchRegion(id + "F50", true);
            var Q1;
            Q1=sQuery(id+"F50.wireOp",EDGE,"E87");
            revolve(context, id + "F51", {"entities" : qUnion([Q0]), "axis" : qUnion([Q1]), "revolveType" : RevolveType.FULL});
        }
        {
            var Q0;
            Q0=makeQuery(id+"F51.opRevolve","SWEPT_BODY",BODY,{"disambiguationData":[OSD([sQuery(id+"F50.wireOp",EDGE,"E87"),sQuery(id+"F50.wireOp",EDGE,"E88"),sQuery(id+"F50.wireOp",EDGE,"E89"),sQuery(id+"F50.wireOp",EDGE,"E90"),sQuery(id+"F50.wireOp",EDGE,"E91"),sQuery(id+"F50.wireOp",EDGE,"E93"),sQuery(id+"F50.wireOp",EDGE,"E94"),sQuery(id+"F50.wireOp",EDGE,"E95.0.0")])]});
            var Q1;
            Q1=makeQuery(id+"F1.opExtrude","SWEPT_BODY",BODY,{"disambiguationData":[OSD([sQuery(id+"F0.wireOp",EDGE,"E0.bottom"),sQuery(id+"F0.wireOp",EDGE,"E0.top"),sQuery(id+"F0.wireOp",EDGE,"E0.left"),sQuery(id+"F0.wireOp",EDGE,"E0.right")])]});
            booleanBodies(context, id + "F52", {"operationType" : BooleanOperationType.SUBTRACTION, "tools" : qUnion([Q0]), "targets" : qUnion([Q1]), "keepTools" : true});
        }
        {
            var Q0;
            Q0=makeQuery(id+"F51.opRevolve","SWEPT_BODY",BODY,{"disambiguationData":[OSD([sQuery(id+"F50.wireOp",EDGE,"E87"),sQuery(id+"F50.wireOp",EDGE,"E88"),sQuery(id+"F50.wireOp",EDGE,"E89"),sQuery(id+"F50.wireOp",EDGE,"E90"),sQuery(id+"F50.wireOp",EDGE,"E91"),sQuery(id+"F50.wireOp",EDGE,"E93"),sQuery(id+"F50.wireOp",EDGE,"E94"),sQuery(id+"F50.wireOp",EDGE,"E95.0.0")])]});
            var Q1;
            Q1=makeQuery(id+"F27.opLoft","SWEPT_BODY",BODY,{"disambiguationData":[OSD([makeQuery(id+"F24.imprint","IMPRINT",FACE,{"disambiguationData":[TD([[makeQuery(id+"F24.imprint","IMPRINT",EDGE,{"derivedFrom":sQuery(id+"F24.wireOp",EDGE,"E43")}),1.0]])]}),makeQuery(id+"F26.imprint","IMPRINT",FACE,{"disambiguationData":[TD([[makeQuery(id+"F26.imprint","IMPRINT",EDGE,{"derivedFrom":sQuery(id+"F26.wireOp",EDGE,"E46")}),-1.0]])]})])]});
            booleanBodies(context, id + "F53", {"operationType" : BooleanOperationType.SUBTRACTION, "tools" : qUnion([Q0]), "targets" : qUnion([Q1]), "keepTools" : true});
        }
    });
